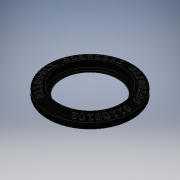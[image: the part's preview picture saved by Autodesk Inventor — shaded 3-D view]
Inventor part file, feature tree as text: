
AUTODESK INVENTOR PART (.ipt)
format: ipt  version: 2016 (Build 200138000, 138)  size: 1,367,552 bytes
history: native  units: in
note: dims shown in document units (in); Inventor stores cm internally (conversion verified against a paired STEP export)
features: sketch x2, revolve x1, extrude x1, projected_geometry x1
ambient origin geometry x8: Origin, YZ Plane, XZ Plane, XY Plane, X Axis, Y Axis, Z Axis, Center Point
bodies: Solid1 (feature_tree)
feature tree (5):
  revolve  "Revolution1"  [1 undecoded]
  extrude  "Extrusion1"  Depth=0.1in
  sketch  "Sketch1"  dims[d0=0.8265in d1=0.175in]
  sketch  "Sketch2"  dims[d2=0.05in d3=0.1in d4=0.15in d5=0.275in d6=90.0deg d7=0.075in d8=1.0in d9=0.0in]
  projected_geometry  "Projected Loop1"
note: 1 required parameter value undecoded (feature->parameter linkage not recoverable at this tier; creation-order binding heuristic only, values carry confidence <= 0.55)
